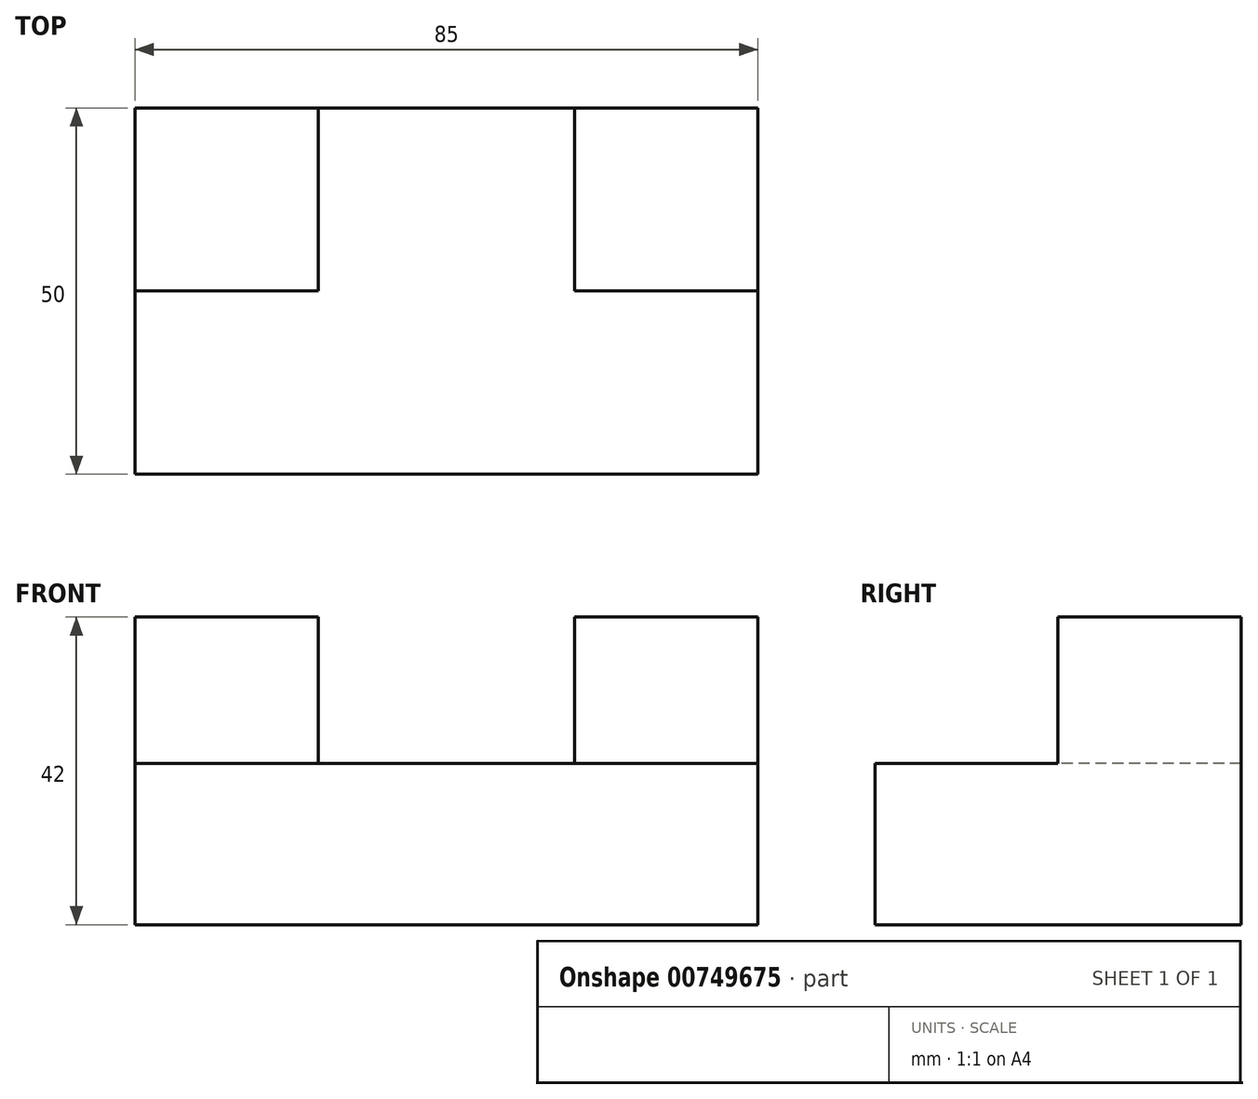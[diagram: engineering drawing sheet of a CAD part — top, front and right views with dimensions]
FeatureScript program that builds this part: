
annotation { "Feature Type Name" : "Feature", "Feature Type Description" : "" }
export const myFeature = defineFeature(function(context is Context, id is Id, definition is map)
    precondition{}
    {
        {
            var Q0;
            Q0=qCreatedBy(makeId("Top.planeOp"),FACE);
            var sketch = newSketch(context, id + "F0", { "sketchPlane" : qUnion([Q0])});
            skLineSegment(sketch, "E0.bottom", {"start": v(-85, 50) * mm, "end": v(0, 50) * mm});
            skLineSegment(sketch, "E0.top", {"start": v(-85, 0) * mm, "end": v(0, 0) * mm});
            skLineSegment(sketch, "E0.left", {"start": v(-85, 50) * mm, "end": v(-85, 0) * mm});
            skLineSegment(sketch, "E0.right", {"start": v(0, 50) * mm, "end": v(0, 0) * mm});
            skLineSegment(sketch, "E1", {"start": v(-60, 50) * mm, "end": v(-60, 25) * mm});
            skLineSegment(sketch, "E2", {"start": v(-60, 25) * mm, "end": v(-85, 25) * mm});
            skLineSegment(sketch, "E3", {"start": v(-25, 50) * mm, "end": v(-25, 25) * mm});
            skLineSegment(sketch, "E4", {"start": v(-25, 25) * mm, "end": v(0, 25) * mm});
            skSolve(sketch);
        }
        {
            var Q0;
            Q0 = qSketchRegion(id + "F0", true);
            extrude(context, id + "F1", {"entities" : qUnion([Q0]), "oppositeDirection" : true, "depth" : 22 * mm, "offsetDistance" : 25 * mm});
        }
        {
            var Q0;
            {var subQ3=sQuery(id+"F0.wireOp",EDGE,"E1");Q0=makeQuery(id+"F0.imprint","IMPRINT",FACE,{"disambiguationData":[TD([[makeQuery(id+"F0.imprint","IMPRINT",EDGE,{"derivedFrom":subQ3}),-1.0]])]});}
            var Q1;
            {var subQ3=sQuery(id+"F0.wireOp",EDGE,"E3");Q1=makeQuery(id+"F0.imprint","IMPRINT",FACE,{"disambiguationData":[TD([[makeQuery(id+"F0.imprint","IMPRINT",EDGE,{"derivedFrom":subQ3}),1.0]])]});}
            extrude(context, id + "F2", {"entities" : qUnion([Q0, Q1]), "operationType" : NewBodyOperationType.ADD, "depth" : 20 * mm, "offsetDistance" : 25 * mm});
        }
    });
